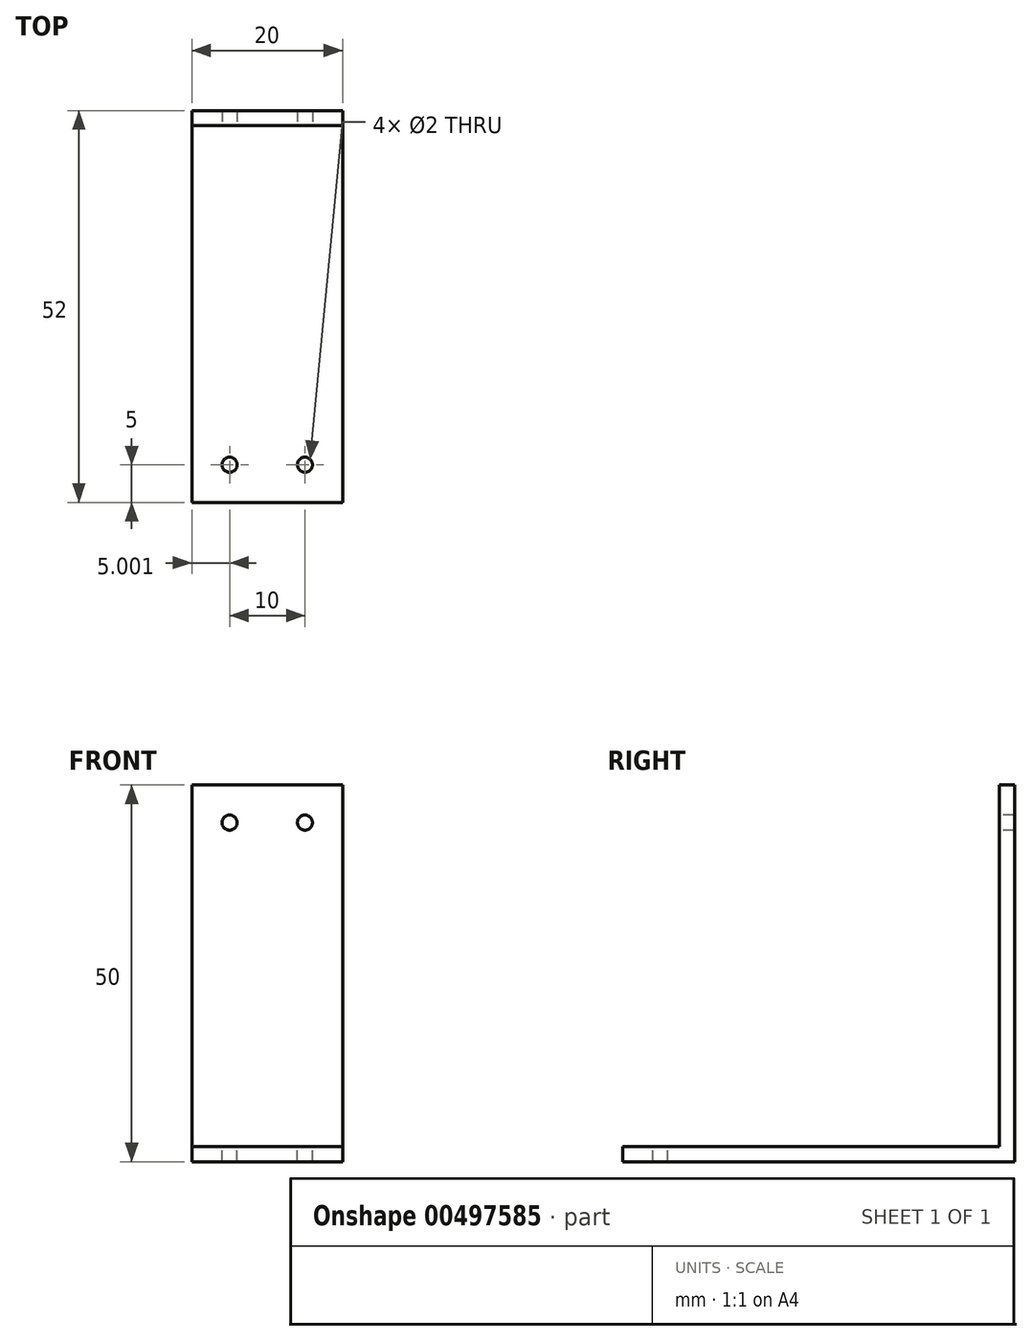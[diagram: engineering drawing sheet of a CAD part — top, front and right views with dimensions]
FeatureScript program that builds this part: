
annotation { "Feature Type Name" : "Feature", "Feature Type Description" : "" }
export const myFeature = defineFeature(function(context is Context, id is Id, definition is map)
    precondition{}
    {
        {
            var Q0;
            Q0=qCreatedBy(makeId("Front.planeOp"),FACE);
            var sketch = newSketch(context, id + "F0", { "sketchPlane" : qUnion([Q0])});
            skLineSegment(sketch, "E0.bottom", {"start": v(-23.13, 23.04) * mm, "end": v(-3.13, 23.04) * mm});
            skLineSegment(sketch, "E0.top", {"start": v(-23.13, -26.96) * mm, "end": v(-3.13, -26.96) * mm});
            skLineSegment(sketch, "E0.left", {"start": v(-23.13, 23.04) * mm, "end": v(-23.13, -26.96) * mm});
            skLineSegment(sketch, "E0.right", {"start": v(-3.13, 23.04) * mm, "end": v(-3.13, -26.96) * mm});
            skSolve(sketch);
        }
        {
            var Q0;
            Q0=makeQuery(id+"F0.imprint","IMPRINT",FACE,{"disambiguationData":[TD([[makeQuery(id+"F0.imprint","IMPRINT",EDGE,{"derivedFrom":sQuery(id+"F0.wireOp",EDGE,"E0.bottom")}),-1.0]])]});
            extrude(context, id + "F1", {"entities" : qUnion([Q0]), "depth" : 2 * mm});
        }
        {
            var Q0;
            Q0=makeQuery(id+"F1.opExtrude","CAP_FACE",FACE,{"disambiguationData":[OSD([sQuery(id+"F0.wireOp",EDGE,"E0.bottom"),sQuery(id+"F0.wireOp",EDGE,"E0.top"),sQuery(id+"F0.wireOp",EDGE,"E0.left"),sQuery(id+"F0.wireOp",EDGE,"E0.right")])],"isStart":false});
            var sketch = newSketch(context, id + "F2", { "sketchPlane" : qUnion([Q0])});
            skLineSegment(sketch, "E1.bottom", {"start": v(-23.13, -24.96) * mm, "end": v(-3.13, -24.96) * mm});
            skLineSegment(sketch, "E1.top", {"start": v(-23.13, -26.96) * mm, "end": v(-3.13, -26.96) * mm});
            skLineSegment(sketch, "E1.left", {"start": v(-23.13, -24.96) * mm, "end": v(-23.13, -26.96) * mm});
            skLineSegment(sketch, "E1.right", {"start": v(-3.13, -24.96) * mm, "end": v(-3.13, -26.96) * mm});
            skSolve(sketch);
        }
        {
            var Q0;
            Q0=makeQuery(id+"F2.imprint","IMPRINT",FACE,{"disambiguationData":[TD([[makeQuery(id+"F2.imprint","IMPRINT",EDGE,{"derivedFrom":sQuery(id+"F2.wireOp",EDGE,"E1.bottom")}),-1.0]])]});
            extrude(context, id + "F3", {"entities" : qUnion([Q0]), "operationType" : NewBodyOperationType.ADD, "depth" : 50 * mm});
        }
        {
            var Q0;
            Q0=makeQuery(id+"F1.opExtrude","CAP_FACE",FACE,{"disambiguationData":[OSD([sQuery(id+"F0.wireOp",EDGE,"E0.bottom"),sQuery(id+"F0.wireOp",EDGE,"E0.top"),sQuery(id+"F0.wireOp",EDGE,"E0.left"),sQuery(id+"F0.wireOp",EDGE,"E0.right")])],"isStart":false});
            var sketch = newSketch(context, id + "F4", { "sketchPlane" : qUnion([Q0])});
            skCircle(sketch, "E2", {"center": v(-18.13, 18.04) * mm, "radius": 1 * mm});
            skSolve(sketch);
        }
        {
            var Q0;
            Q0 = qSketchRegion(id + "F4", true);
            extrude(context, id + "F5", {"entities" : qUnion([Q0]), "operationType" : NewBodyOperationType.REMOVE, "oppositeDirection" : true, "depth" : 2 * mm});
        }
        {
            var Q0;
            Q0=makeQuery(id+"F1.opExtrude","CAP_FACE",FACE,{"disambiguationData":[OSD([sQuery(id+"F0.wireOp",EDGE,"E0.bottom"),sQuery(id+"F0.wireOp",EDGE,"E0.top"),sQuery(id+"F0.wireOp",EDGE,"E0.left"),sQuery(id+"F0.wireOp",EDGE,"E0.right")])],"isStart":false});
            var sketch = newSketch(context, id + "F6", { "sketchPlane" : qUnion([Q0])});
            skCircle(sketch, "E3", {"center": v(-8.13, 18.04) * mm, "radius": 1 * mm});
            skSolve(sketch);
        }
        {
            var Q0;
            Q0 = qSketchRegion(id + "F6", true);
            extrude(context, id + "F7", {"entities" : qUnion([Q0]), "operationType" : NewBodyOperationType.REMOVE, "oppositeDirection" : true, "depth" : 2 * mm});
        }
        {
            var Q0;
            Q0=makeQuery(id+"F3.opExtrude","SWEPT_FACE",FACE,{"disambiguationData":[OSD([sQuery(id+"F2.wireOp",EDGE,"E1.bottom")])]});
            var sketch = newSketch(context, id + "F8", { "sketchPlane" : qUnion([Q0])});
            skCircle(sketch, "E4", {"center": v(-8.13, -47) * mm, "radius": 1 * mm});
            skCircle(sketch, "E5", {"center": v(-18.13, -47) * mm, "radius": 1 * mm});
            skSolve(sketch);
        }
        {
            var Q0;
            Q0 = qSketchRegion(id + "F8", true);
            extrude(context, id + "F9", {"entities" : qUnion([Q0]), "operationType" : NewBodyOperationType.REMOVE, "oppositeDirection" : true, "depth" : 2 * mm});
        }
        {
            var Q0;
            Q0=makeQuery(id+"F1.opExtrude","SWEPT_BODY",BODY,{"disambiguationData":[OSD([sQuery(id+"F0.wireOp",EDGE,"E0.bottom"),sQuery(id+"F0.wireOp",EDGE,"E0.top"),sQuery(id+"F0.wireOp",EDGE,"E0.left"),sQuery(id+"F0.wireOp",EDGE,"E0.right")])]});
            transform(context, id + "F10", {"entities" : qUnion([Q0]), "transformType" : TransformType.TRANSLATION_3D, "dx" : 0 * mm, "dy" : 0 * mm, "dz" : 0 * mm, "makeCopy" : true});
        }
    });
